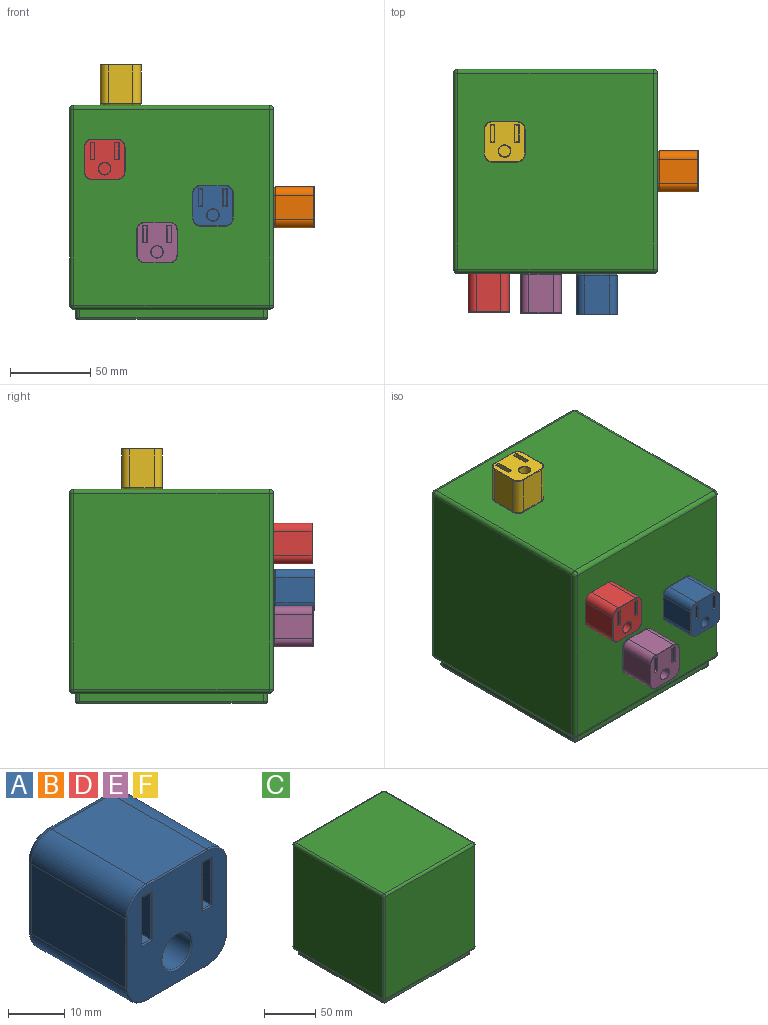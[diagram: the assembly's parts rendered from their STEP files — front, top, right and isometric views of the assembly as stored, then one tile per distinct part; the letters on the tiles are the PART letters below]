
ASSEMBLY  parts=6 mates=2
PART A: 47 faces, bbox 26.2x25.4x26.2 mm
  f0: plane 24.89x24.89mm, normal (0,-1,0), area 490.5mm2, adj f30,f31,f32,f33,f34,f35,f36,f37
  f1: plane 23.88x15.24mm, normal (0,0,1), area 363.9mm2, adj f18,f21,f28,f35
  f2: plane 23.88x15.24mm, normal (-1,0,0), area 363.9mm2, adj f18,f19,f27,f36
  f3: plane 23.88x15.24mm, normal (0,0,-1), area 363.9mm2, adj f19,f20,f23,f32
  f4: plane 23.88x15.24mm, normal (1,0,0), area 363.9mm2, adj f20,f21,f24,f31
  f5: plane 22.86x22.86mm, normal (0,1,0), area 510.1mm2, adj f22,f23,f24,f25,f26,f27,f28,f29
  f6: cylinder r=3.69mm len=15.24mm, axis (0,-1,0), area 353.1mm2, adj f7,f38
  f7: plane 7.38x7.38mm, normal (0,-1,0), area 42.7mm2, adj f6
  f8: plane 15.24x10.33mm, normal (1,0,0), area 157.5mm2, adj f9,f11,f12,f39
  f9: plane 15.24x2.28mm, normal (0,0,1), area 34.7mm2, adj f8,f10,f12,f40
  f10: plane 15.24x10.33mm, normal (-1,0,0), area 157.5mm2, adj f9,f11,f12,f42
  f11: plane 15.24x2.28mm, normal (0,0,-1), area 34.7mm2, adj f8,f10,f12,f41
  f12: plane 10.33x2.28mm, normal (0,-1,0), area 23.5mm2, adj f8,f9,f10,f11
  f13: plane 15.24x2.28mm, normal (0,0,-1), area 34.7mm2, adj f14,f16,f17,f45
  f14: plane 15.24x10.33mm, normal (1,0,0), area 157.5mm2, adj f13,f15,f17,f46
  f15: plane 15.24x2.28mm, normal (0,0,1), area 34.7mm2, adj f14,f16,f17,f44
  f16: plane 15.24x10.33mm, normal (-1,0,0), area 157.5mm2, adj f13,f15,f17,f43
  f17: plane 10.33x2.28mm, normal (0,-1,0), area 23.5mm2, adj f13,f14,f15,f16
  f18: cylinder r=5.08mm len=23.88mm, axis (0,-1,0), area 190.5mm2, adj f1,f2,f29,f37
  f19: cylinder r=5.08mm len=23.88mm, axis (0,1,0), area 190.5mm2, adj f2,f3,f25,f34
  f20: cylinder r=5.08mm len=23.88mm, axis (0,-1,0), area 190.5mm2, adj f3,f4,f22,f30
  f21: cylinder r=5.08mm len=23.88mm, axis (0,1,0), area 190.5mm2, adj f1,f4,f26,f33
  f22: torus R=3.81mm, axis (0,-1,0), area 14.5mm2, adj f5,f20,f23,f24
  f23: cylinder r=1.27mm len=15.24mm, axis (1,0,0), area 30.4mm2, adj f3,f5,f22,f25
  f24: cylinder r=1.27mm len=15.24mm, axis (0,0,1), area 30.4mm2, adj f4,f5,f22,f26
  f25: torus R=3.81mm, axis (0,-1,0), area 14.5mm2, adj f5,f19,f23,f27
  f26: torus R=3.81mm, axis (0,-1,0), area 14.5mm2, adj f5,f21,f24,f28
  f27: cylinder r=1.27mm len=15.24mm, axis (0,0,-1), area 30.4mm2, adj f2,f5,f25,f29
  f28: cylinder r=1.27mm len=15.24mm, axis (-1,0,0), area 30.4mm2, adj f1,f5,f26,f29
  f29: torus R=3.81mm, axis (0,-1,0), area 14.5mm2, adj f5,f18,f27,f28
  f30: torus R=4.83mm, axis (0,-1,0), area 3.1mm2, adj f0,f20,f31,f32
  f31: cylinder r=0.25mm len=15.24mm, axis (0,0,-1), area 6.1mm2, adj f0,f4,f30,f33
  f32: cylinder r=0.25mm len=15.24mm, axis (-1,0,0), area 6.1mm2, adj f0,f3,f30,f34
  f33: torus R=4.83mm, axis (0,-1,0), area 3.1mm2, adj f0,f21,f31,f35
  f34: torus R=4.83mm, axis (0,-1,0), area 3.1mm2, adj f0,f19,f32,f36
  f35: cylinder r=0.25mm len=15.24mm, axis (1,0,0), area 6.1mm2, adj f0,f1,f33,f37
  f36: cylinder r=0.25mm len=15.24mm, axis (0,0,1), area 6.1mm2, adj f0,f2,f34,f37
  f37: torus R=4.83mm, axis (0,-1,0), area 3.1mm2, adj f0,f18,f35,f36
  f38: torus R=3.94mm, axis (0,-1,0), area 9.5mm2, adj f0,f6
  f39: cylinder r=0.25mm len=10.84mm, axis (0,0,1), area 4.2mm2, adj f0,f8,f40,f41
  f40: cylinder r=0.25mm len=2.78mm, axis (-1,0,0), area 1mm2, adj f0,f9,f39,f42
  f41: cylinder r=0.25mm len=2.78mm, axis (1,0,0), area 1mm2, adj f0,f11,f39,f42
  f42: cylinder r=0.25mm len=10.84mm, axis (0,0,-1), area 4.2mm2, adj f0,f10,f40,f41
  f43: cylinder r=0.25mm len=10.84mm, axis (0,0,-1), area 4.2mm2, adj f0,f16,f44,f45
  f44: cylinder r=0.25mm len=2.78mm, axis (-1,0,0), area 1mm2, adj f0,f15,f43,f46
  f45: cylinder r=0.25mm len=2.78mm, axis (1,0,0), area 1mm2, adj f0,f13,f43,f46
  f46: cylinder r=0.25mm len=10.84mm, axis (0,0,1), area 4.2mm2, adj f0,f14,f44,f45
PART B: same geometry as A
PART C: 43 faces, bbox 127x127x133.4 mm
  f0: plane 121.92x121.92mm, normal (0,0,-1), area 618.4mm2, adj f6,f7,f8,f9,f17,f18,f26,f27
  f1: plane 121.92x121.92mm, normal (1,0,0), area 14864.5mm2, adj f19,f24,f27,f30
  f2: plane 121.92x121.92mm, normal (0,1,0), area 14864.5mm2, adj f16,f25,f26,f30
  f3: plane 121.92x121.92mm, normal (-1,0,0), area 14864.5mm2, adj f11,f15,f16,f17
  f4: plane 121.92x121.92mm, normal (0,-1,0), area 14864.5mm2, adj f11,f14,f18,f19
  f5: plane 121.92x121.92mm, normal (0,0,1), area 14864.5mm2, adj f14,f15,f24,f25
  f6: plane 114.3x5.08mm, normal (-1,0,0), area 580.6mm2, adj f0,f31,f34,f40
  f7: plane 114.3x5.08mm, normal (0,1,0), area 580.6mm2, adj f0,f31,f32,f41
  f8: plane 114.3x5.08mm, normal (1,0,0), area 580.6mm2, adj f0,f32,f33,f37
  f9: plane 114.3x5.08mm, normal (0,-1,0), area 580.6mm2, adj f0,f33,f34,f36
  f10: plane 116.84x116.84mm, normal (0,0,-1), area 13650.2mm2, adj f35,f36,f37,f38,f39,f40,f41,f42
  f11: cylinder r=2.54mm len=121.92mm, axis (0,0,1), area 486.4mm2, adj f3,f4,f12,f13
  f12: sphere r=2.54mm, area 10.1mm2, adj f11,f14,f15
  f13: sphere r=2.54mm, area 10.1mm2, adj f11,f17,f18
  f14: cylinder r=2.54mm len=121.92mm, axis (-1,0,0), area 486.4mm2, adj f4,f5,f12,f20
  f15: cylinder r=2.54mm len=121.92mm, axis (0,1,0), area 486.4mm2, adj f3,f5,f12,f21
  f16: cylinder r=2.54mm len=121.92mm, axis (0,0,-1), area 486.4mm2, adj f2,f3,f21,f22
  f17: cylinder r=2.54mm len=121.92mm, axis (0,-1,0), area 486.4mm2, adj f0,f3,f13,f22
  f18: cylinder r=2.54mm len=121.92mm, axis (1,0,0), area 486.4mm2, adj f0,f4,f13,f23
  f19: cylinder r=2.54mm len=121.92mm, axis (0,0,-1), area 486.4mm2, adj f1,f4,f20,f23
  f20: sphere r=2.54mm, area 10.1mm2, adj f14,f19,f24
  f21: sphere r=2.54mm, area 10.1mm2, adj f15,f16,f25
  f22: sphere r=2.54mm, area 10.1mm2, adj f16,f17,f26
  f23: sphere r=2.54mm, area 10.1mm2, adj f18,f19,f27
  f24: cylinder r=2.54mm len=121.92mm, axis (0,-1,0), area 486.4mm2, adj f1,f5,f20,f28
  f25: cylinder r=2.54mm len=121.92mm, axis (1,0,0), area 486.4mm2, adj f2,f5,f21,f28
  f26: cylinder r=2.54mm len=121.92mm, axis (-1,0,0), area 486.4mm2, adj f0,f2,f22,f29
  f27: cylinder r=2.54mm len=121.92mm, axis (0,1,0), area 486.4mm2, adj f0,f1,f23,f29
  f28: sphere r=2.54mm, area 10.1mm2, adj f24,f25,f30
  f29: sphere r=2.54mm, area 10.1mm2, adj f26,f27,f30
  f30: cylinder r=2.54mm len=121.92mm, axis (0,0,1), area 486.4mm2, adj f1,f2,f28,f29
  f31: cylinder r=2.54mm len=5.08mm, axis (0,0,1), area 20.3mm2, adj f0,f6,f7,f42
  f32: cylinder r=2.54mm len=5.08mm, axis (0,0,-1), area 20.3mm2, adj f0,f7,f8,f39
  f33: cylinder r=2.54mm len=5.08mm, axis (0,0,1), area 20.3mm2, adj f0,f8,f9,f35
  f34: cylinder r=2.54mm len=5.08mm, axis (0,0,-1), area 20.3mm2, adj f0,f6,f9,f38
  f35: torus R=1.27mm, axis (0,0,-1), area 6.5mm2, adj f10,f33,f36,f37
  f36: cylinder r=1.27mm len=114.3mm, axis (1,0,0), area 228mm2, adj f9,f10,f35,f38
  f37: cylinder r=1.27mm len=114.3mm, axis (0,1,0), area 228mm2, adj f8,f10,f35,f39
  f38: torus R=1.27mm, axis (0,0,-1), area 6.5mm2, adj f10,f34,f36,f40
  f39: torus R=1.27mm, axis (0,0,-1), area 6.5mm2, adj f10,f32,f37,f41
  f40: cylinder r=1.27mm len=114.3mm, axis (0,-1,0), area 228mm2, adj f6,f10,f38,f42
  f41: cylinder r=1.27mm len=114.3mm, axis (-1,0,0), area 228mm2, adj f7,f10,f39,f42
  f42: torus R=1.27mm, axis (0,0,-1), area 6.5mm2, adj f10,f31,f40,f41
PART D: same geometry as A
PART E: same geometry as A
PART F: same geometry as A
PLACE A t=(14.61,-36.9,54.19)mm
PLACE B rot(axis=(0,0,1),90deg) t=(52.38,26.96,53.24)mm
PLACE C t=(-11.12,26.96,-10.26)mm
PLACE D t=(-52.81,-35.5,83.07)mm
PLACE E t=(-20.18,-36.02,31.29)mm
PLACE F rot(axis=(-1,0,0),90deg) t=(-42.87,45.25,116.74)mm
MATE fastened B.f5 <-> C.f1  axis (-1,0,0) through (52.38,26.96,53.24)mm
MATE planar F.f5 <-> C.f5  axis (0,0,-1) through (-42.87,45.25,116.74)mm
